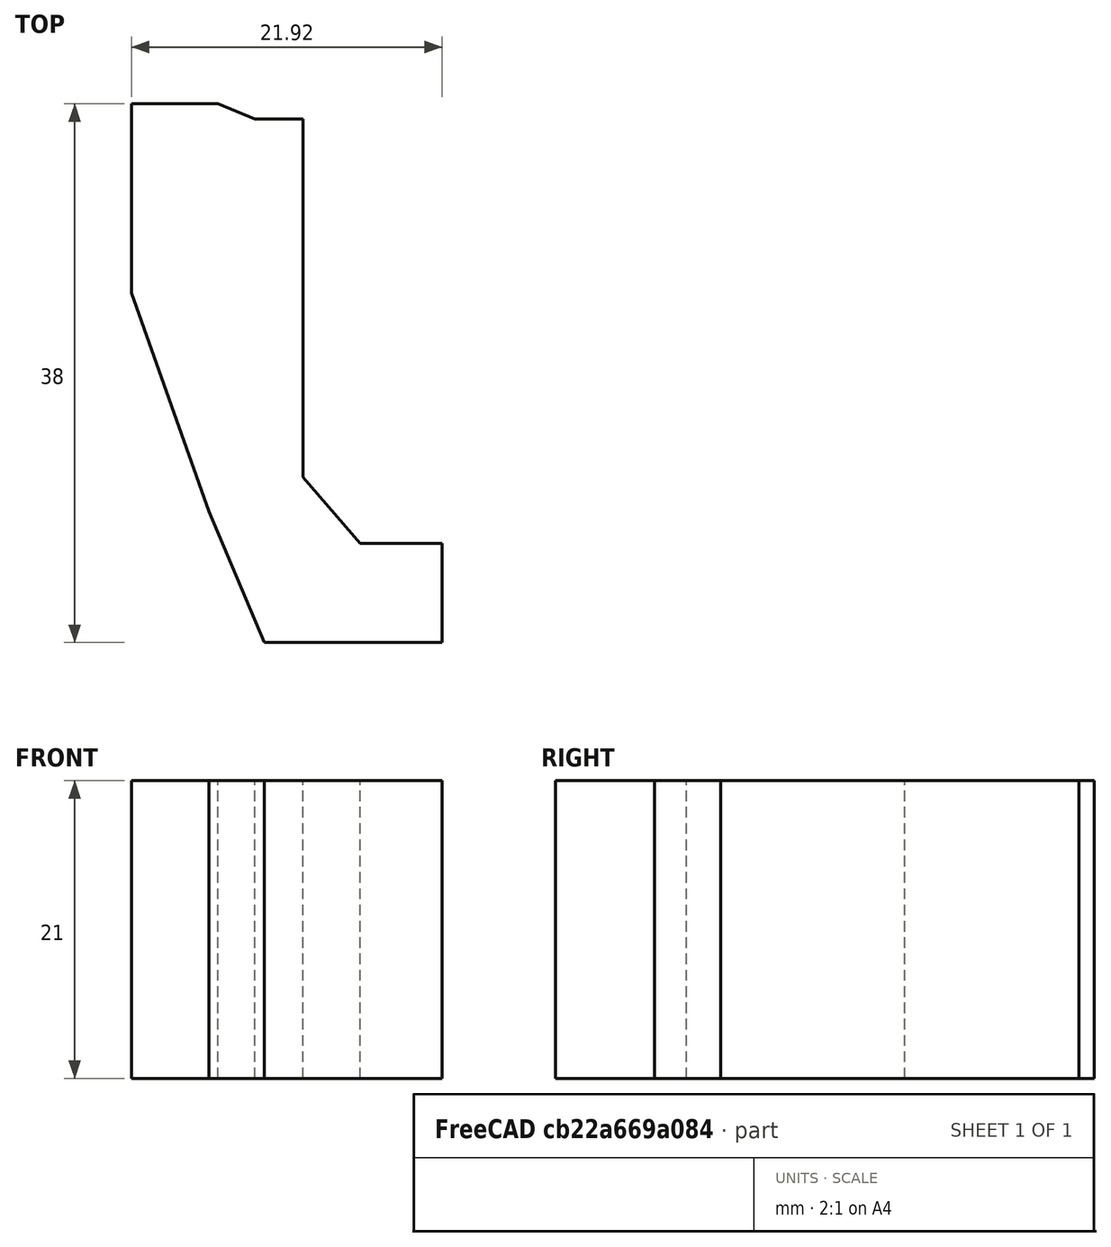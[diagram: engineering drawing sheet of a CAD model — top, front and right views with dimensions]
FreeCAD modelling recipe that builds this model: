
FCSTD DOCUMENT  (FreeCAD 0.22R35329 (Git))
Label: sprite extruder se ptfe mount
License: All rights reserved
LicenseURL: https://en.wikipedia.org/wiki/All_rights_reserved
objects: Sketcher::SketchObject×1, Image::ImagePlane×1, PartDesign::Pad×1, PartDesign::Body×1
note: 4 computed .brp shape members not serialized (recipe doc carries the construction recipe); baked Part::Feature solids carry a one-line shape summary decoded from their .brp

FEATURE [Sketcher::SketchObject] Sketch
  FullyConstrained = false
  MapMode = 5
  Support = -> [XY_Plane]
  sketch-geometry (11):
    g0: LineSegment StartX=15.0642 StartY=13.7633 StartZ=0 EndX=15.0642 EndY=-11.5295 EndZ=0
    g1: LineSegment StartX=19.0774 StartY=-16.168 StartZ=0 EndX=24.8617 EndY=-16.168 EndZ=0
    g2: LineSegment StartX=15.0642 StartY=-11.5295 StartZ=0 EndX=19.0774 EndY=-16.168 EndZ=0
    g3: LineSegment StartX=24.8617 StartY=-16.168 StartZ=0 EndX=24.8617 EndY=-23.168 EndZ=0
    g4: LineSegment StartX=24.8617 StartY=-23.168 StartZ=0 EndX=12.3217 EndY=-23.168 EndZ=0
    g5: LineSegment StartX=12.3217 StartY=-23.168 StartZ=0 EndX=8.41961 EndY=-13.9252 EndZ=0
    g6: LineSegment StartX=8.41961 StartY=-13.9252 StartZ=0 EndX=2.93783 EndY=1.47661 EndZ=0
    g7: LineSegment StartX=2.93783 StartY=1.47661 StartZ=0 EndX=2.93783 EndY=14.8283 EndZ=0
    g8: LineSegment StartX=2.93783 StartY=14.8283 StartZ=0 EndX=9.04229 EndY=14.8283 EndZ=0
    g9: LineSegment StartX=9.04229 StartY=14.8283 StartZ=0 EndX=11.6467 EndY=13.7633 EndZ=0
    g10: LineSegment StartX=11.6467 StartY=13.7633 StartZ=0 EndX=15.0642 EndY=13.7633 EndZ=0
  constraints (19):
    c: Vertical(g0)
    c: Horizontal(g1)
    c: Coincident(g2,g0)
    c: Coincident(g2,g1)
    c: Coincident(g3,g1)
    c: Vertical(g3)
    c: Coincident(g3,g4)
    c: Horizontal(g4)
    c: Coincident(g4,g5)
    c: Coincident(g5,g6)
    c: Coincident(g6,g7)
    c: Vertical(g7)
    c: Coincident(g7,g8)
    c: Horizontal(g8)
    c: Coincident(g8,g9)
    c: Coincident(g9,g10)
    c: Coincident(g10,g0)
    c: Horizontal(g10)
    c: DistanceY(g3,g3) = 7
FEATURE [Image::ImagePlane] _0231209_174925  label="20231209_174925"
  Placement = pos=(0,0,0) rot=(0,0,-1;0.008727rad)
  XSize = 142.954
  YSize = 107.216
FEATURE [PartDesign::Pad] Pad
  Direction = (0,0,1)
  Length = 21
  Length2 = 10
  Profile = -> Sketch
  ReferenceAxis = -> Sketch [N_Axis]
  Type = 0
FEATURE [PartDesign::Body] Body
  Group = -> [Sketch,Pad]
  Origin = -> Origin
  Tip = -> Pad
